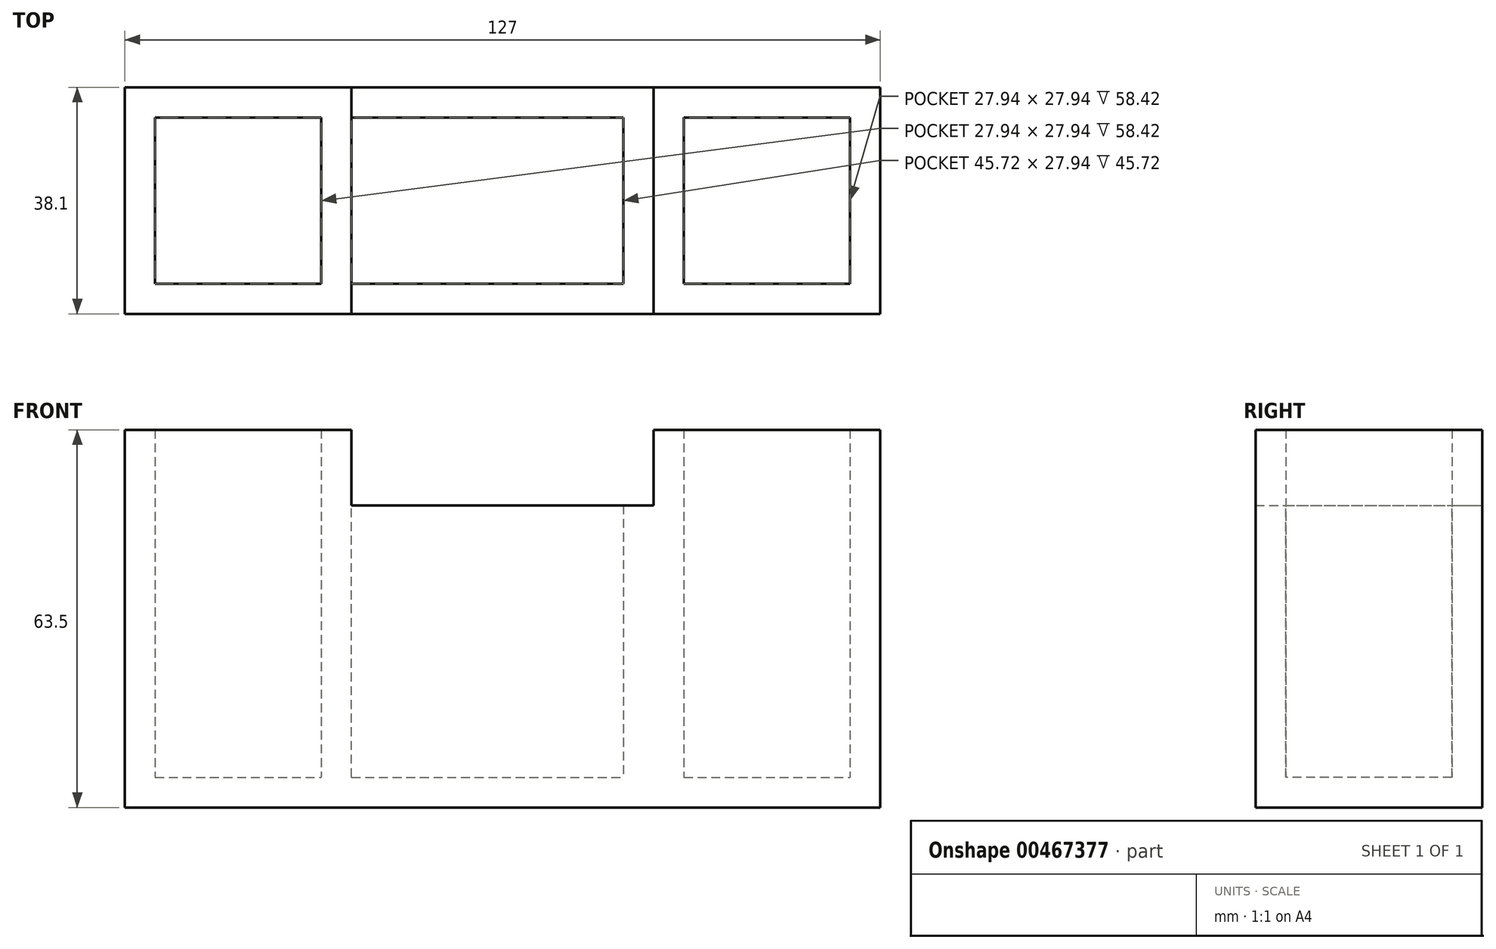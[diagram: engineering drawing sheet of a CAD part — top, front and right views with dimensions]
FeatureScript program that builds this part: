
annotation { "Feature Type Name" : "Feature", "Feature Type Description" : "" }
export const myFeature = defineFeature(function(context is Context, id is Id, definition is map)
    precondition{}
    {
        {
            var Q0;
            Q0=qCreatedBy(makeId("Top.planeOp"),FACE);
            var sketch = newSketch(context, id + "F0", { "sketchPlane" : qUnion([Q0])});
            skLineSegment(sketch, "E0.bottom", {"start": v(-63.5, 19.05) * mm, "end": v(63.5, 19.05) * mm});
            skLineSegment(sketch, "E0.top", {"start": v(-63.5, -19.05) * mm, "end": v(63.5, -19.05) * mm});
            skLineSegment(sketch, "E0.left", {"start": v(-63.5, 19.05) * mm, "end": v(-63.5, -19.05) * mm});
            skLineSegment(sketch, "E0.right", {"start": v(63.5, 19.05) * mm, "end": v(63.5, -19.05) * mm});
            skPoint(sketch, "E0.middle", {"position": v(0, 0) * mm});
            skLineSegment(sketch, "E1", {"start": v(-25.4, -19.05) * mm, "end": v(-25.4, 19.05) * mm});
            skLineSegment(sketch, "E2", {"start": v(25.4, -19.05) * mm, "end": v(25.4, 19.05) * mm});
            skLineSegment(sketch, "E3", {"start": v(30.48, -19.05) * mm, "end": v(30.48, 19.05) * mm});
            skSolve(sketch);
        }
        {
            var Q0;
            {var subQ0=sQuery(id+"F0.wireOp",EDGE,"E0.left");Q0=makeQuery(id+"F0.imprint","IMPRINT",FACE,{"disambiguationData":[TD([[makeQuery(id+"F0.imprint","IMPRINT",EDGE,{"derivedFrom":subQ0}),1.0]])]});}
            extrude(context, id + "F1", {"entities" : qUnion([Q0]), "depth" : 63.5 * mm});
        }
        {
            var Q0;
            Q0=makeQuery(id+"F1.opExtrude","CAP_FACE",FACE,{"disambiguationData":[OSD([sQuery(id+"F0.wireOp",EDGE,"E0.bottom"),sQuery(id+"F0.wireOp",EDGE,"E0.top"),sQuery(id+"F0.wireOp",EDGE,"E0.left"),sQuery(id+"F0.wireOp",EDGE,"E1")])],"isStart":false});
            shell(context, id + "F2", {"entities" : qUnion([Q0]), "thickness" : 5.08 * mm});
        }
        {
            var Q0;
            {var subQ0=sQuery(id+"F0.wireOp",EDGE,"E1");Q0=makeQuery(id+"F0.imprint","IMPRINT",FACE,{"disambiguationData":[TD([[makeQuery(id+"F0.imprint","IMPRINT",EDGE,{"derivedFrom":subQ0}),-1.0]])]});}
            extrude(context, id + "F3", {"entities" : qUnion([Q0]), "operationType" : NewBodyOperationType.ADD, "depth" : 50.8 * mm});
        }
        {
            var Q0;
            {var subQ0=sQuery(id+"F0.wireOp",EDGE,"E0.right");Q0=makeQuery(id+"F0.imprint","IMPRINT",FACE,{"disambiguationData":[TD([[makeQuery(id+"F0.imprint","IMPRINT",EDGE,{"derivedFrom":subQ0}),-1.0]])]});}
            extrude(context, id + "F4", {"entities" : qUnion([Q0]), "operationType" : NewBodyOperationType.ADD, "depth" : 63.5 * mm});
        }
        {
            var Q0;
            Q0=makeQuery(id+"F3.opExtrude","CAP_FACE",FACE,{"disambiguationData":[OSD([sQuery(id+"F0.wireOp",EDGE,"E0.bottom"),sQuery(id+"F0.wireOp",EDGE,"E0.top"),sQuery(id+"F0.wireOp",EDGE,"E1"),sQuery(id+"F0.wireOp",EDGE,"E2")])],"isStart":false});
            shell(context, id + "F5", {"entities" : qUnion([Q0]), "thickness" : 5.08 * mm});
        }
        {
            var Q0;
            Q0=makeQuery(id+"F4.opExtrude","SWEPT_BODY",BODY,{"disambiguationData":[OSD([sQuery(id+"F0.wireOp",EDGE,"E0.bottom"),sQuery(id+"F0.wireOp",EDGE,"E0.top"),sQuery(id+"F0.wireOp",EDGE,"E0.right"),sQuery(id+"F0.wireOp",EDGE,"E3")])]});
            deleteBodies(context, id + "F6", {"entities" : qUnion([Q0])});
        }
        {
            var Q0;
            {var subQ0=sQuery(id+"F0.wireOp",EDGE,"E2");Q0=makeQuery(id+"F0.imprint","IMPRINT",FACE,{"disambiguationData":[TD([[makeQuery(id+"F0.imprint","IMPRINT",EDGE,{"derivedFrom":subQ0}),-1.0]])]});}
            extrude(context, id + "F7", {"entities" : qUnion([Q0]), "operationType" : NewBodyOperationType.ADD, "depth" : 63.5 * mm});
        }
        {
            var Q0;
            {var subQ0=sQuery(id+"F0.wireOp",EDGE,"E0.right");Q0=makeQuery(id+"F0.imprint","IMPRINT",FACE,{"disambiguationData":[TD([[makeQuery(id+"F0.imprint","IMPRINT",EDGE,{"derivedFrom":subQ0}),-1.0]])]});}
            extrude(context, id + "F8", {"entities" : qUnion([Q0]), "operationType" : NewBodyOperationType.ADD, "depth" : 63.5 * mm});
        }
        {
            var Q0;
            {var subQ0=sQuery(id+"F0.wireOp",EDGE,"E3");var subQ1=sQuery(id+"F0.wireOp",EDGE,"E0.top");var subQ2=sQuery(id+"F0.wireOp",EDGE,"E0.bottom");Q0=makeQuery(id+"F8.boolean.opBoolean","MERGE",FACE,{"derivedFrom":[makeQuery(id+"F7.opExtrude","CAP_FACE",FACE,{"disambiguationData":[OSD([subQ2,subQ1,sQuery(id+"F0.wireOp",EDGE,"E2"),subQ0])],"isStart":false}),makeQuery(id+"F8.opExtrude","CAP_FACE",FACE,{"disambiguationData":[OSD([subQ2,subQ1,sQuery(id+"F0.wireOp",EDGE,"E0.right"),subQ0])],"isStart":false})]});}
            shell(context, id + "F9", {"entities" : qUnion([Q0]), "thickness" : 5.08 * mm});
        }
        {
            var Q0;
            {var subQ0=sQuery(id+"F0.wireOp",EDGE,"E2");Q0=makeQuery(id+"F0.imprint","IMPRINT",FACE,{"disambiguationData":[TD([[makeQuery(id+"F0.imprint","IMPRINT",EDGE,{"derivedFrom":subQ0}),-1.0]])]});}
            extrude(context, id + "F10", {"entities" : qUnion([Q0]), "operationType" : NewBodyOperationType.ADD, "depth" : 50.8 * mm});
        }
    });
